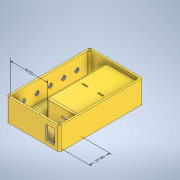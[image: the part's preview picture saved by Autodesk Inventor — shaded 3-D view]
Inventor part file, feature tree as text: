
AUTODESK INVENTOR PART (.ipt)
format: ipt  version: 2020 (Build 240168000, 168)  size: 323,072 bytes
history: native  units: mm
features: sketch x13, extrude x11, other x3, fillet x3, hole x3, projected_geometry x2
ambient origin geometry x8: Origin, YZ Plane, XZ Plane, XY Plane, X Axis, Y Axis, Z Axis, Center Point
bodies: Solid1 (feature_tree)
feature tree (35):
  other  "Annotations"
  extrude  "Extrusion1"  Depth=110.0mm
  extrude  "Extrusion2"  Depth=105.0mm
  sketch  "Sketch3"  dims[d4=30.0mm d5=0.0mm d6=3.0mm d7=0.0mm]
  extrude  "Extrusion3"  Depth=3.0mm TaperAngle=0.0deg
  extrude  "Extrusion4"  Depth=78.0mm
  extrude  "Extrusion5"  Depth=76.0mm
  fillet  "Fillet1"  Radius=25.0mm
  extrude  "Extrusion6"  Depth=2.0mm TaperAngle=0.0deg
  extrude  "Extrusion7"  Depth=3.0mm
  extrude  "Extrusion8"  Depth=3.0mm
  fillet  "Fillet2"  Radius=1.5mm
  hole  "Hole1"  [1 undecoded]
  fillet  "Fillet3"  Radius=2.0mm
  extrude  "Extrusion9"  Depth=30.0mm TaperAngle=0.0deg
  extrude  "Extrusion10"  Depth=2.0mm
  hole  "Hole3"  [1 undecoded]
  hole  "Hole4"  [1 undecoded]
  extrude  "Extrusion11"  Depth=2.0mm
  sketch  "Sketch1"  dims[d0=70.0mm d1=110.0mm]
  sketch  "Sketch2"  dims[d2=65.0mm d3=105.0mm]
  sketch  "Sketch4"  dims[d8=44.0mm d9=78.0mm]
  sketch  "Sketch5"  dims[d10=41.5mm d11=76.0mm d12=25.0mm d13=0.0mm]
  sketch  "Sketch6"  dims[d14=25.0mm d15=0.0mm d16=2.0mm d17=0.0mm]
  sketch  "Sketch7"  dims[d18=2.0mm d19=3.0mm]
  sketch  "Sketch8"  dims[d20=1.5mm d21=3.0mm d22=1.5mm]
  sketch  "Sketch9"  dims[d23=2.0mm d24=0.0mm d25=3.0mm d26=2.0mm]
  sketch  "Sketch10"  dims[d27=2.0mm d28=0.0mm d29=30.0mm d30=0.0mm]
  sketch  "Sketch12"  dims[d31=2.0mm]
  sketch  "Sketch14"  dims[d32=3.0mm d33=6.0mm d34=4.0mm d35=2.0mm d36=90.0deg d37=40.0mm d38=20.594885mm d39=2.0mm]
  sketch  "Sketch16"  dims[d40=2.0mm d41=2.0mm d42=2.0mm d43=2.0mm d44=2.0mm d45=2.0mm d46=2.0mm d47=0.0mm d48=15.0mm d49=1.5mm d50=0.0mm d58=3.75mm d59=90.0deg d60=1.0mm d61=6.0mm d62=3.5mm d63=2.0mm d64=90.0deg d65=1.0mm d66=20.594885mm d71=17.6mm d72=50.0mm d74=17.6mm d75=10.0mm d77=10.0mm d79=18.0mm d80=5.5mm d81=6.0mm d82=3.5mm d83=2.0mm d84=90.0deg d85=3.0mm d86=0.0mm d88=4.0mm d89=180.0deg d90=12.0mm d91=19.0mm d92=3.0mm d93=0.0mm d69=6.515894mm d70=27.0mm d94=15.238305mm d95=9.122444mm d96=49.5mm]
  projected_geometry  "Project Cut Edges1"
  projected_geometry  "Project Cut Edges2"
  other  "Linear Dimension 1"
  other  "Linear Dimension 2"
note: 3 required parameter values undecoded (feature->parameter linkage not recoverable at this tier; creation-order binding heuristic only, values carry confidence <= 0.55)
